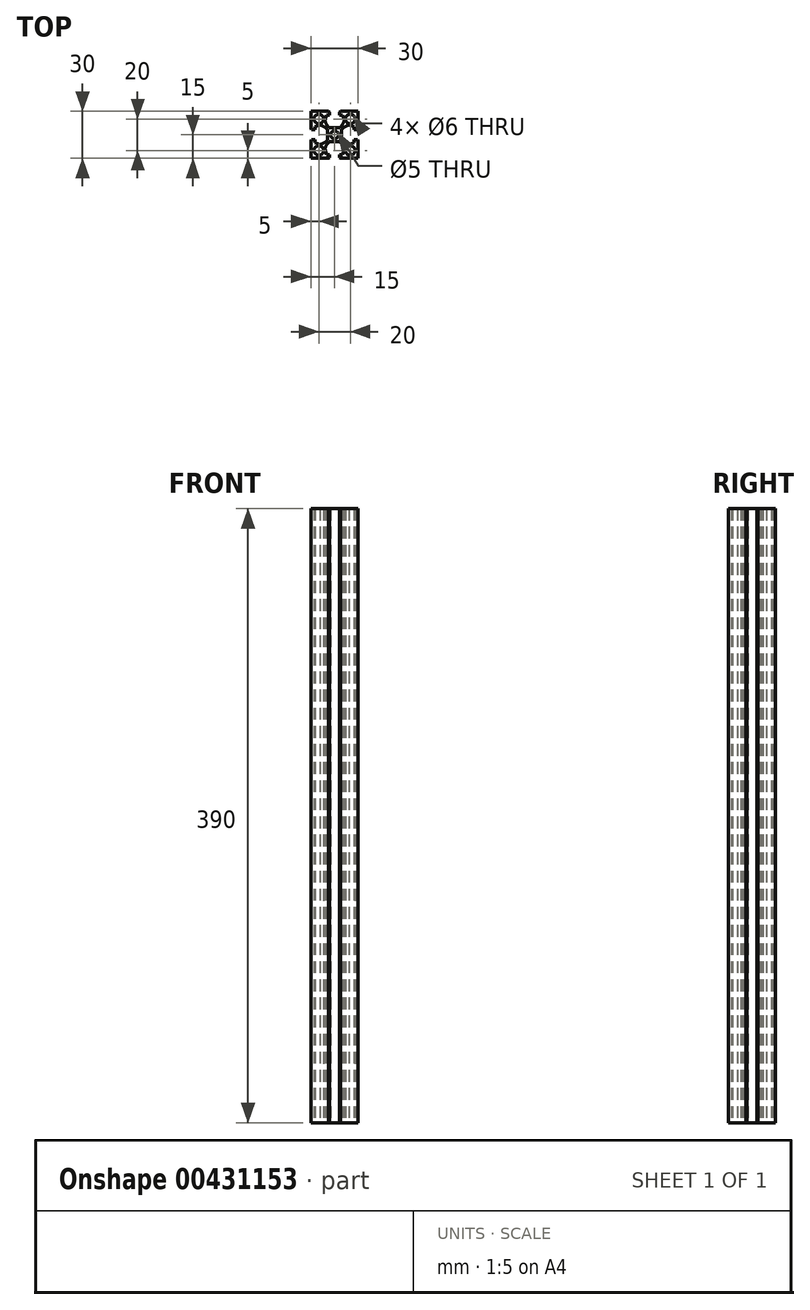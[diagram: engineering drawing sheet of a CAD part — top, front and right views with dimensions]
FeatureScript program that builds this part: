
annotation { "Feature Type Name" : "Feature", "Feature Type Description" : "" }
export const myFeature = defineFeature(function(context is Context, id is Id, definition is map)
    precondition{}
    {
        {
            var Q0;
            Q0=qCreatedBy(makeId("Top.planeOp"),FACE);
            var sketch = newSketch(context, id + "F0", { "sketchPlane" : qUnion([Q0])});
            skLineSegment(sketch, "E0.bottom", {"start": v(15, 15) * mm, "end": v(3.95, 15) * mm});
            skLineSegment(sketch, "E0.top", {"start": v(15, -15) * mm, "end": v(3.95, -15) * mm});
            skLineSegment(sketch, "E0.left", {"start": v(15, 15) * mm, "end": v(15, 3.95) * mm});
            skLineSegment(sketch, "E0.right", {"start": v(-15, 15) * mm, "end": v(-15, 3.95) * mm});
            skPoint(sketch, "E0.middle", {"position": v(0, 0) * mm});
            skLineSegment(sketch, "E1", {"start": v(0, 15) * mm, "end": v(0, -15) * mm, "construction": true});
            skLineSegment(sketch, "E2", {"start": v(-15, 0) * mm, "end": v(15, 0) * mm, "construction": true});
            skCircle(sketch, "E3", {"center": v(-10, 10) * mm, "radius": 3 * mm});
            skCircle(sketch, "E4", {"center": v(0, 0) * mm, "radius": 2.5 * mm});
            skLineSegment(sketch, "E5", {"start": v(0, 15) * mm, "end": v(0, 12.5) * mm, "construction": true});
            skLineSegment(sketch, "E6", {"start": v(-3.15, 14.5) * mm, "end": v(-3.15, 12.5) * mm});
            skLineSegment(sketch, "E7", {"start": v(-3.15, 12.5) * mm, "end": v(-5.1, 12.5) * mm});
            skLineSegment(sketch, "E8", {"start": v(0, 0) * mm, "end": v(-3.44, 0) * mm, "construction": true});
            skLineSegment(sketch, "E9", {"start": v(-5.1, 12.5) * mm, "end": v(-6.18, 9.16) * mm});
            skLineSegment(sketch, "E10", {"start": v(-3.44, 4.5) * mm, "end": v(0, 4.5) * mm});
            skLineSegment(sketch, "E11", {"start": v(3.36, 15) * mm, "end": v(3.36, 11.64) * mm, "construction": true});
            skArc(sketch, "E12", {"start": v(-3.44, 4.5) * mm, "mid": v(-5.13, 6.64) * mm, "end": v(-6.18, 9.16) * mm});
            skLineSegment(sketch, "E13", {"start": v(-3.95, 15) * mm, "end": v(-3.15, 14.5) * mm});
            skLineSegment(sketch, "E14.trimOffspring", {"start": v(-3.95, 15) * mm, "end": v(-5.1, 15) * mm, "construction": true});
            skLineSegment(sketch, "E15", {"start": v(-15, 15) * mm, "end": v(15, -15) * mm, "construction": true});
            skLineSegment(sketch, "E16", {"start": v(15, 15) * mm, "end": v(-15, -15) * mm, "construction": true});
            skArc(sketch, "E17.MirrorCS", {"start": v(-4.5, 3.43) * mm, "mid": v(-6.64, 5.13) * mm, "end": v(-9.16, 6.18) * mm});
            skLineSegment(sketch, "E18.MirrorCS", {"start": v(-4.5, 3.43) * mm, "end": v(-4.5, 0) * mm});
            skLineSegment(sketch, "E19.MirrorCS", {"start": v(-12.5, 5.1) * mm, "end": v(-9.16, 6.18) * mm});
            skLineSegment(sketch, "E20.MirrorCS", {"start": v(-12.5, 3.15) * mm, "end": v(-12.5, 5.1) * mm});
            skLineSegment(sketch, "E21.MirrorCS", {"start": v(-15, 3.95) * mm, "end": v(-14.5, 3.15) * mm});
            skLineSegment(sketch, "E22.MirrorCS", {"start": v(-14.5, 3.15) * mm, "end": v(-12.5, 3.15) * mm});
            skLineSegment(sketch, "E23.MirrorCS", {"start": v(-14.5, -3.15) * mm, "end": v(-12.5, -3.15) * mm});
            skLineSegment(sketch, "E24.MirrorCS", {"start": v(-15, -3.95) * mm, "end": v(-14.5, -3.15) * mm});
            skLineSegment(sketch, "E25.MirrorCS", {"start": v(-12.5, -3.15) * mm, "end": v(-12.5, -5.1) * mm});
            skLineSegment(sketch, "E26.MirrorCS", {"start": v(-12.5, -5.1) * mm, "end": v(-9.16, -6.18) * mm});
            skArc(sketch, "E27.MirrorCS", {"start": v(-4.5, -3.43) * mm, "mid": v(-6.64, -5.13) * mm, "end": v(-9.16, -6.18) * mm});
            skLineSegment(sketch, "E28.MirrorCS", {"start": v(-4.5, -3.43) * mm, "end": v(-4.5, 0) * mm});
            skLineSegment(sketch, "E29.MirrorCS", {"start": v(-3.44, -4.5) * mm, "end": v(0, -4.5) * mm});
            skArc(sketch, "E30.MirrorCS", {"start": v(-3.44, -4.5) * mm, "mid": v(-5.13, -6.64) * mm, "end": v(-6.18, -9.16) * mm});
            skLineSegment(sketch, "E31.MirrorCS", {"start": v(-5.1, -12.5) * mm, "end": v(-6.18, -9.16) * mm});
            skLineSegment(sketch, "E32.MirrorCS", {"start": v(-3.15, -12.5) * mm, "end": v(-5.1, -12.5) * mm});
            skLineSegment(sketch, "E33.MirrorCS", {"start": v(-3.95, -15) * mm, "end": v(-3.15, -14.5) * mm});
            skLineSegment(sketch, "E34.MirrorCS", {"start": v(-3.15, -14.5) * mm, "end": v(-3.15, -12.5) * mm});
            skLineSegment(sketch, "E35.MirrorCS", {"start": v(3.44, -4.5) * mm, "end": v(0, -4.5) * mm});
            skArc(sketch, "E36.MirrorCS", {"start": v(3.44, -4.5) * mm, "mid": v(5.13, -6.64) * mm, "end": v(6.18, -9.16) * mm});
            skLineSegment(sketch, "E37.MirrorCS", {"start": v(5.1, -12.5) * mm, "end": v(6.18, -9.16) * mm});
            skLineSegment(sketch, "E38.MirrorCS", {"start": v(3.15, -12.5) * mm, "end": v(5.1, -12.5) * mm});
            skLineSegment(sketch, "E39.MirrorCS", {"start": v(3.15, -14.5) * mm, "end": v(3.15, -12.5) * mm});
            skLineSegment(sketch, "E40.MirrorCS", {"start": v(3.95, -15) * mm, "end": v(3.15, -14.5) * mm});
            skArc(sketch, "E41.MirrorCS", {"start": v(4.5, -3.43) * mm, "mid": v(6.64, -5.13) * mm, "end": v(9.16, -6.18) * mm});
            skLineSegment(sketch, "E42.MirrorCS", {"start": v(4.5, 3.44) * mm, "end": v(4.5, 0) * mm});
            skLineSegment(sketch, "E43.MirrorCS", {"start": v(4.5, -3.43) * mm, "end": v(4.5, 0) * mm});
            skArc(sketch, "E44.MirrorCS", {"start": v(4.5, 3.44) * mm, "mid": v(6.64, 5.13) * mm, "end": v(9.16, 6.18) * mm});
            skLineSegment(sketch, "E45.MirrorCS", {"start": v(12.5, 5.1) * mm, "end": v(9.16, 6.18) * mm});
            skLineSegment(sketch, "E46.MirrorCS", {"start": v(12.5, -5.1) * mm, "end": v(9.16, -6.18) * mm});
            skLineSegment(sketch, "E47.MirrorCS", {"start": v(12.5, -3.15) * mm, "end": v(12.5, -5.1) * mm});
            skLineSegment(sketch, "E48.MirrorCS", {"start": v(14.5, -3.15) * mm, "end": v(12.5, -3.15) * mm});
            skLineSegment(sketch, "E49.MirrorCS", {"start": v(12.5, 3.15) * mm, "end": v(12.5, 5.1) * mm});
            skLineSegment(sketch, "E50.MirrorCS", {"start": v(14.5, 3.15) * mm, "end": v(12.5, 3.15) * mm});
            skLineSegment(sketch, "E51.MirrorCS", {"start": v(15, 3.95) * mm, "end": v(14.5, 3.15) * mm});
            skLineSegment(sketch, "E52.MirrorCS", {"start": v(15, -3.95) * mm, "end": v(14.5, -3.15) * mm});
            skLineSegment(sketch, "E53.MirrorCS", {"start": v(3.43, 4.5) * mm, "end": v(0, 4.5) * mm});
            skArc(sketch, "E54.MirrorCS", {"start": v(3.43, 4.5) * mm, "mid": v(5.13, 6.64) * mm, "end": v(6.18, 9.16) * mm});
            skLineSegment(sketch, "E55.MirrorCS", {"start": v(5.1, 12.5) * mm, "end": v(6.18, 9.16) * mm});
            skLineSegment(sketch, "E56.MirrorCS", {"start": v(3.15, 12.5) * mm, "end": v(5.1, 12.5) * mm});
            skLineSegment(sketch, "E57.MirrorCS", {"start": v(3.15, 14.5) * mm, "end": v(3.15, 12.5) * mm});
            skLineSegment(sketch, "E58.MirrorCS", {"start": v(3.95, 15) * mm, "end": v(3.15, 14.5) * mm});
            skCircle(sketch, "E59.MirrorC", {"center": v(10, 10) * mm, "radius": 3 * mm});
            skCircle(sketch, "E60.MirrorC", {"center": v(10, -10) * mm, "radius": 3 * mm});
            skCircle(sketch, "E61.MirrorC", {"center": v(-10, -10) * mm, "radius": 3 * mm});
            skLineSegment(sketch, "E62.trimOffspring", {"start": v(-15, -3.95) * mm, "end": v(-15, -15) * mm});
            skPoint(sketch, "E63.orphan", {"position": v(-15, 3.15) * mm});
            skPoint(sketch, "E64.orphan", {"position": v(-15, -3.15) * mm});
            skLineSegment(sketch, "E65.trimOffspring", {"start": v(-3.95, -15) * mm, "end": v(-15, -15) * mm});
            skPoint(sketch, "E66.orphan", {"position": v(-3.15, -15) * mm});
            skPoint(sketch, "E67.orphan", {"position": v(3.15, -15) * mm});
            skLineSegment(sketch, "E68.trimOffspring", {"start": v(15, -3.95) * mm, "end": v(15, -15) * mm});
            skPoint(sketch, "E69.orphan", {"position": v(15, 3.15) * mm});
            skPoint(sketch, "E70.orphan", {"position": v(15, -3.15) * mm});
            skPoint(sketch, "E71.trimOffspring.end.orphan", {"position": v(3.15, 15) * mm});
            skLineSegment(sketch, "E72.trimOffspring", {"start": v(-3.95, 15) * mm, "end": v(-15, 15) * mm});
            skPoint(sketch, "E73.trimOffspring.end.orphan", {"position": v(-3.15, 15) * mm});
            skSolve(sketch);
        }
        {
            var Q0;
            Q0=makeQuery(id+"F0.imprint","IMPRINT",FACE,{"disambiguationData":[TD([[makeQuery(id+"F0.imprint","IMPRINT",EDGE,{"derivedFrom":sQuery(id+"F0.wireOp",EDGE,"E0.bottom")}),1.0]])]});
            extrude(context, id + "F1", {"entities" : qUnion([Q0]), "endBound" : BoundingType.SYMMETRIC, "depth" : 390 * mm});
        }
    });
